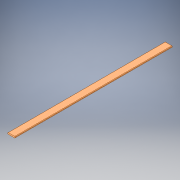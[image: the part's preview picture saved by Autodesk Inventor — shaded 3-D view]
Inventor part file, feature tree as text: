
AUTODESK INVENTOR PART (.ipt)
format: ipt  version: 2019 (Build 230136000, 136)  size: 104,448 bytes
history: native  units: in
note: dims shown in document units (in); Inventor stores cm internally (conversion verified against a paired STEP export)
features: extrude x1, fillet x1, sketch x1
ambient origin geometry x8: Origin, YZ Plane, XZ Plane, XY Plane, X Axis, Y Axis, Z Axis, Center Point
bodies: Solid1 (feature_tree)
feature tree (3):
  extrude  "Extrusion1"  Depth=1.1024in
  fillet  "Fillet1"  Radius=118.1102in
  sketch  "Sketch1"  dims[d0=5.5118in d1=1.1024in d2=118.1102in d3=0.0in d4=0.315in]
